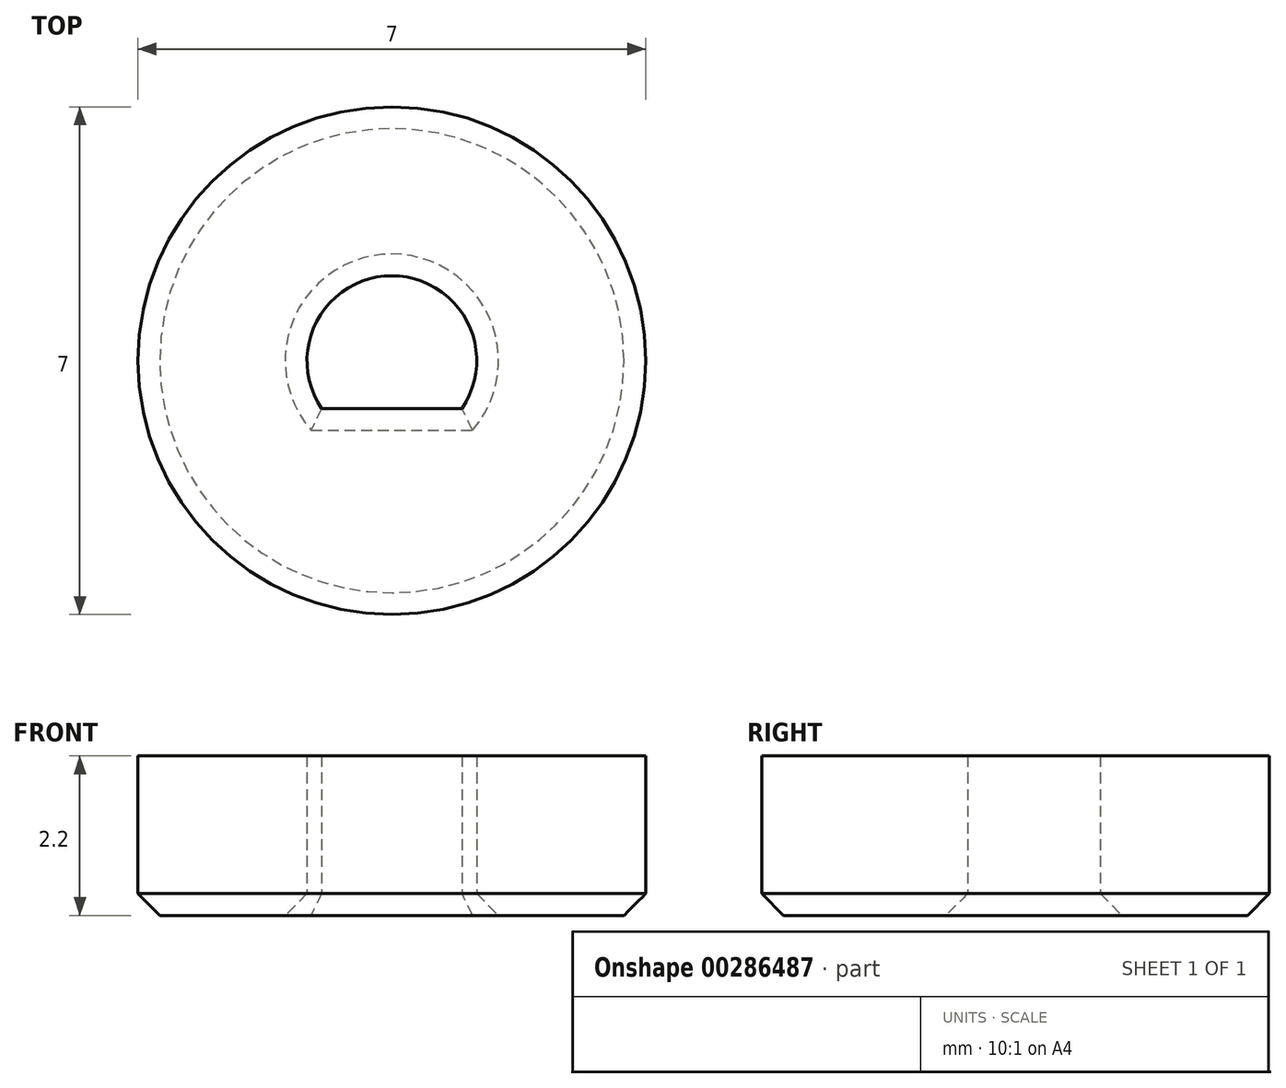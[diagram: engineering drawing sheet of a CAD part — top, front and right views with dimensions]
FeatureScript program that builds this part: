
annotation { "Feature Type Name" : "Feature", "Feature Type Description" : "" }
export const myFeature = defineFeature(function(context is Context, id is Id, definition is map)
    precondition{}
    {
        {
            var Q0;
            Q0=qCreatedBy(makeId("Top.planeOp"),FACE);
            var sketch = newSketch(context, id + "F0", { "sketchPlane" : qUnion([Q0])});
            skArc(sketch, "E0", {"start": v(0.85, -0.46) * mm, "mid": v(0, 0.97) * mm, "end": v(-0.85, -0.46) * mm});
            skCircle(sketch, "E1", {"center": v(0, 0) * mm, "radius": 3.5 * mm});
            skLineSegment(sketch, "E2", {"start": v(-0.85, -0.46) * mm, "end": v(0.85, -0.46) * mm});
            skArc(sketch, "E3.0", {"start": v(0.97, -0.66) * mm, "mid": v(0, 1.17) * mm, "end": v(-0.97, -0.66) * mm});
            skLineSegment(sketch, "E3.1", {"start": v(-0.97, -0.66) * mm, "end": v(0.97, -0.66) * mm});
            skSolve(sketch);
        }
        {
            var Q0;
            Q0=makeQuery(id+"F0.imprint","IMPRINT",FACE,{"disambiguationData":[TD([[makeQuery(id+"F0.imprint","IMPRINT",EDGE,{"derivedFrom":sQuery(id+"F0.wireOp",EDGE,"E1")}),1.0]])]});
            extrude(context, id + "F1", {"entities" : qUnion([Q0]), "depth" : 2.2 * mm, "offsetDistance" : 25 * mm});
        }
        {
            var Q0;
            Q0=makeQuery(id+"F1.opExtrude","CAP_FACE",FACE,{"disambiguationData":[OSD([sQuery(id+"F0.wireOp",EDGE,"E1"),sQuery(id+"F0.wireOp",EDGE,"E3.0"),sQuery(id+"F0.wireOp",EDGE,"E3.1")])],"isStart":true});
            chamfer(context, id + "F2", {"entities" : qUnion([Q0]), "width" : .3 * mm, "tangentPropagation" : true});
        }
    });
